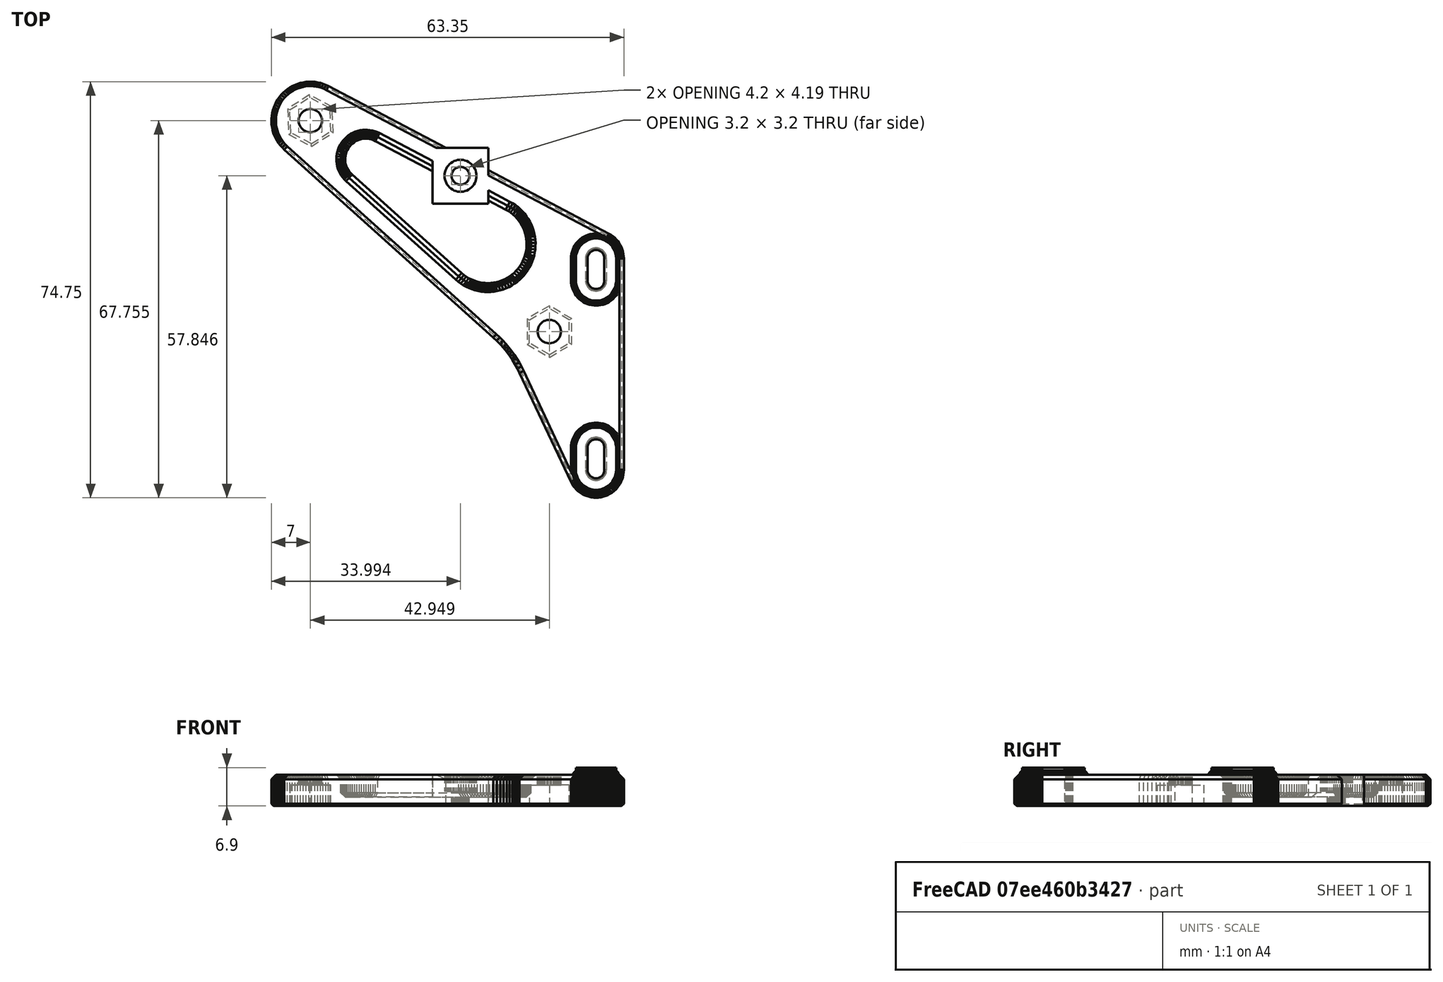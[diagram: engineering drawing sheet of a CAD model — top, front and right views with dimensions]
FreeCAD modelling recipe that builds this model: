
FCSTD DOCUMENT  (FreeCAD 2021.1015R24301 +3962 (Git))
Label: Duct_Mount_Plate_Right
License: All rights reserved
LicenseURL: http://en.wikipedia.org/wiki/All_rights_reserved
objects: Part::Feature×1, Part::Refine×1, App::DocumentObjectGroup×1, PartDesign::FeatureBase×1, PartDesign::SubShapeBinder×1, PartDesign::Pad×1, PartDesign::Body×1
note: 9 computed .brp shape members not serialized (recipe doc carries the construction recipe); baked Part::Feature solids carry a one-line shape summary decoded from their .brp

FEATURE [Part::Feature] Duct_Mount_Plate_Right001_solid  label="Duct_Mount_Plate_Right001 (Solid)"
  shape: bbox 63.35 x 74.75 x 6.4 mm, 6246 faces (baked)
FEATURE [Part::Refine] Refined  label="Duct_Mount_Plate_Right001 (Solid)001"
  Source = -> Duct_Mount_Plate_Right001_solid
FEATURE [App::DocumentObjectGroup] Group  label="sources"
  ExportMode = 1
  Group = -> [Duct_Mount_Plate_Right001_solid,Refined]
  _GroupVersion = 1
FEATURE [PartDesign::FeatureBase] BaseFeature001
  BaseFeature = -> Refined
  NewSolid = false
  Suppress = false
FEATURE [PartDesign::SubShapeBinder] Binder  label="Binder(BaseFeature001)..."
  BindCopyOnChange = 0
  BindMode = 0
  ClaimChildren = false
  Context = -> Body [Binder.]
  FillStyle = 0
  Fuse = false
  MakeFace = true
  PartialLoad = false
  Relative = true
  Support = -> [BaseFeature001[Face4122,Face4123]]
  _Version = 7
FEATURE [PartDesign::Pad] Pad
  BaseFeature = -> BaseFeature001
  ClaimChildren = false
  Direction = (1,1,1)
  Fit = 0
  FitJoin = 0
  InnerFit = 0
  InnerFitJoin = 0
  InnerTaperAngle = 0
  InnerTaperAngleRev = 0
  Length = 0.5
  Length2 = 100
  Linearize = true
  NewSolid = false
  Profile = -> Binder
  Refine = true
  Suppress = false
  Type = 0
  _ProfileBasedVersion = 1
FEATURE [PartDesign::Body] Body  label="Duct Mount Plate Right"
  AutoGroupSolids = false
  BaseFeature = -> Refined
  ExportMode = 0
  Group = -> [BaseFeature001,Binder,Pad]
  Origin = -> Origin
  Tip = -> Pad
  _ExportChildren = -> [BaseFeature001,Pad]
  _GroupVersion = 1
